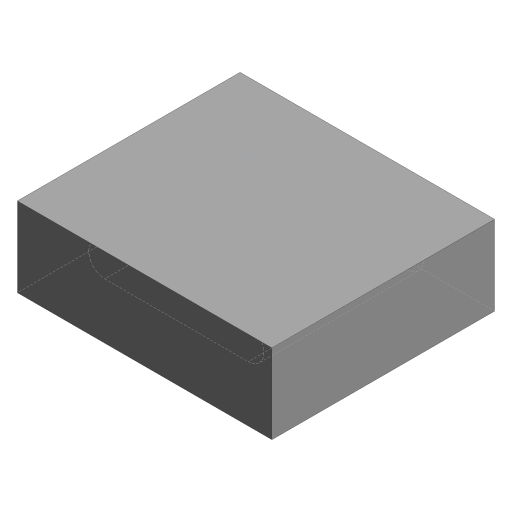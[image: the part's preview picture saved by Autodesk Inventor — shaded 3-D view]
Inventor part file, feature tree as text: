
AUTODESK INVENTOR PART (.ipt)
format: ipt  version: 2023 (Build 270158000, 158)  size: 71,168 bytes
history: native  units: mm (DEFAULTED — no unit token found)
features: sketch x2, extrude x2
ambient origin geometry x8: Origin, YZ Plane, XZ Plane, XY Plane, X Axis, Y Axis, Z Axis, Center Point
bodies: Solid1 (feature_tree)
feature tree (4):
  sketch  "Sketch1"  dims[d0=-15.875mm d1=-22.225mm d2=44.45mm d3=0.0mm]
  extrude  "Extrusion1"  Depth=44.45mm TaperAngle=0.0deg
  extrude  "Extrusion2"  [1 undecoded]
  sketch  "Sketch2"  dims[d4=31.75mm d5=0.0mm]
note: 1 required parameter value undecoded (feature->parameter linkage not recoverable at this tier; creation-order binding heuristic only, values carry confidence <= 0.55)
